# Revit family: QF_TRUE_TSSU-48-18M-B-HC_cat
name_source: partatom
category: Specialty Equipment
revit_build: Autodesk Revit 2016 (Build: 20150714_1515(x64)
units: mm (PartAtom-declared; Revit-internal decimal feet)

## family parameters
Always vertical = Yes
Cut with Voids When Loaded = No
Part Type = Normal
Room Calculation Point = No
Round Connector Dimension = Use Diameter
Shared = No
Work Plane-Based = No

## types (1)
- QF_TRUE_TSSU-48-18M-B-HC_cat
    Apparent Power = 667 VA
    Conn Conduit = Yes
    Conn Plug = NEMA 5-15P
    Cycle = 60 Hz
    Depth = 34 1/16"
    Description = MEGA-TOP SOLID DOOR SANDWICH/SALAD UNIT WITH HYDROCARBON REFRIGERANT
    Elec Conn Connection Height = 0"
    Elec Conn RI Height = 0"
    FL Amps = 6 A
    Foodservice Equipment Identifier = Yes
    HP = 1/3
    Identify Quantity as Lot = Yes
    Length = 48 5/16"
    Manufacturer = TRUE
    Max Overcurrent Protection = 0 A
    Min Ckt Ampacity = 0 A
    Model = TSSU-48-18M-B-HC
    Number of Poles = 1
    Phase = 1
    Volts = 115 V
    Watts = 667 W
    Weight in Pounds = 310

## geometry (parser evidence)
native form markers: Blend x30, Sweep x14
no freeform markers — native parametric forms only
